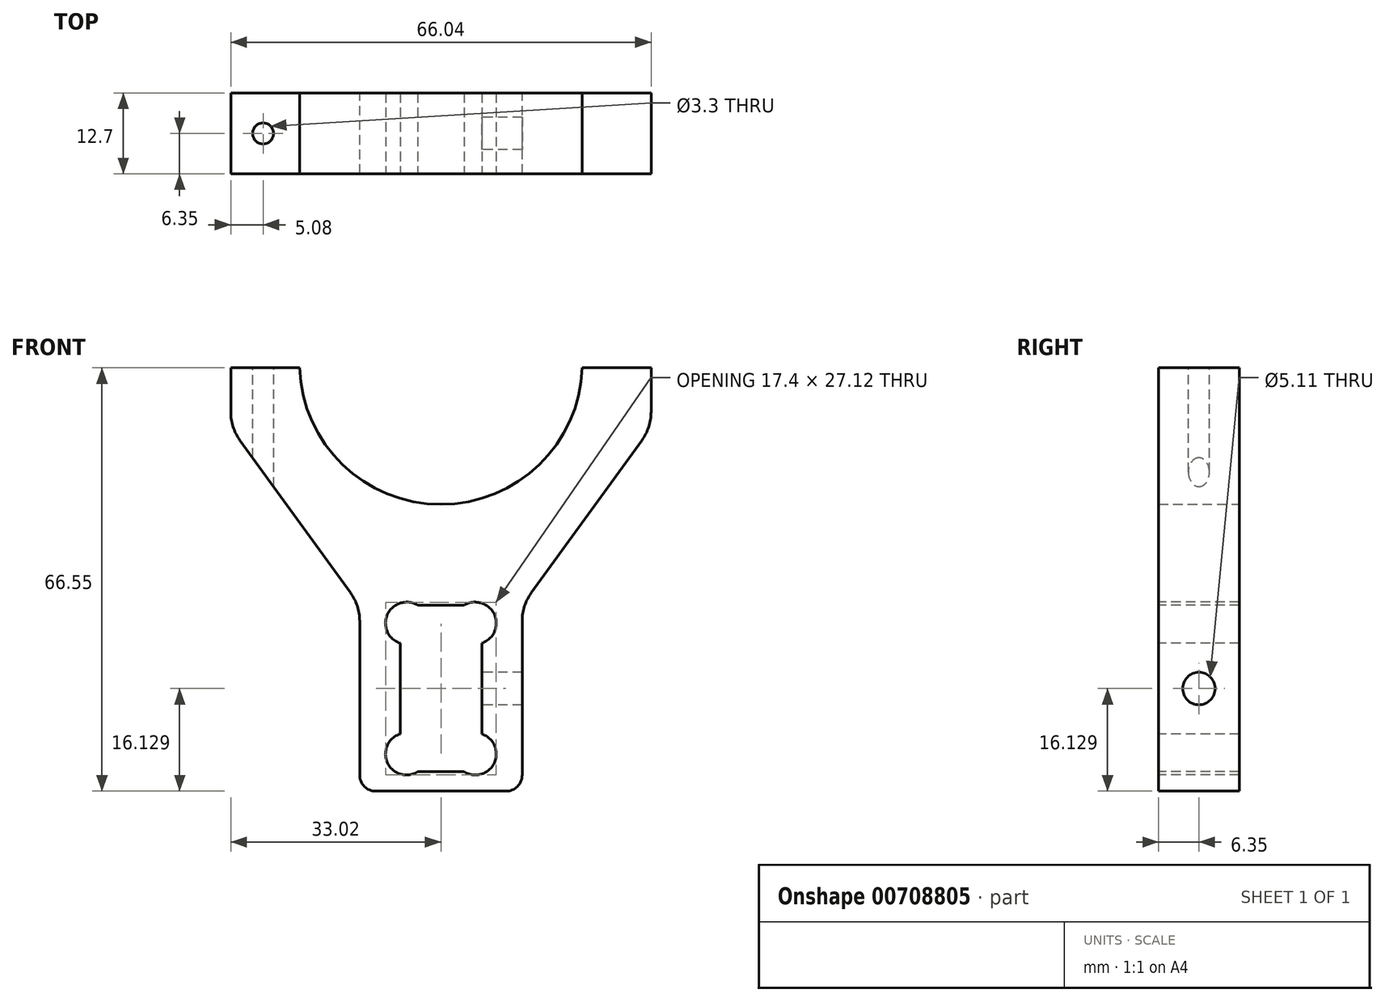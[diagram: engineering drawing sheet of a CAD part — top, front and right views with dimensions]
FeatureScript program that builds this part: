
annotation { "Feature Type Name" : "Feature", "Feature Type Description" : "" }
export const myFeature = defineFeature(function(context is Context, id is Id, definition is map)
    precondition{}
    {
        {
            var Q0;
            Q0=qCreatedBy(makeId("Front.planeOp"),FACE);
            var sketch = newSketch(context, id + "F0", { "sketchPlane" : qUnion([Q0])});
            skLineSegment(sketch, "E0", {"start": v(-6.41, 0) * mm, "end": v(6.41, 0) * mm});
            skLineSegment(sketch, "E1", {"start": v(6.41, 0) * mm, "end": v(6.41, -26.16) * mm});
            skLineSegment(sketch, "E2", {"start": v(12.76, -29.21) * mm, "end": v(12.76, 0) * mm});
            skLineSegment(sketch, "E3", {"start": v(-12.76, 0) * mm, "end": v(-12.76, -29.21) * mm});
            skLineSegment(sketch, "E4", {"start": v(-12.76, -29.21) * mm, "end": v(12.76, -29.21) * mm});
            skLineSegment(sketch, "E5", {"start": v(6.41, -26.16) * mm, "end": v(-6.41, -26.16) * mm});
            skLineSegment(sketch, "E6", {"start": v(-6.41, -26.16) * mm, "end": v(-6.41, 0) * mm});
            skCircle(sketch, "E7", {"center": v(0, 38.1) * mm, "radius": 20 * mm, "construction": true});
            skCircle(sketch, "E8", {"center": v(0, 38.1) * mm, "radius": 32.5 * mm, "construction": true});
            skLineSegment(sketch, "E9", {"start": v(-22.21, 37.34) * mm, "end": v(-33.02, 37.34) * mm});
            skLineSegment(sketch, "E10", {"start": v(-33.02, 37.34) * mm, "end": v(-33.02, 27.94) * mm});
            skLineSegment(sketch, "E11", {"start": v(-33.02, 27.94) * mm, "end": v(-12.76, 0) * mm});
            skLineSegment(sketch, "E12.MirrorCS", {"start": v(33.02, 27.94) * mm, "end": v(12.76, 0) * mm});
            skLineSegment(sketch, "E13.MirrorCS", {"start": v(22.21, 37.34) * mm, "end": v(33.02, 37.34) * mm});
            skLineSegment(sketch, "E14.MirrorCS", {"start": v(33.02, 37.34) * mm, "end": v(33.02, 27.94) * mm});
            skArc(sketch, "E15", {"start": v(-22.21, 37.34) * mm, "mid": v(0, 15.88) * mm, "end": v(22.21, 37.34) * mm});
            skArc(sketch, "E16", {"start": v(22.21, 37.34) * mm, "mid": v(0, 60.33) * mm, "end": v(-22.21, 37.34) * mm, "construction": true});
            skSolve(sketch);
        }
        {
            var Q0;
            Q0 = qSketchRegion(id + "F0", true);
            extrude(context, id + "F1", {"entities" : qUnion([Q0]), "endBound" : BoundingType.SYMMETRIC, "depth" : 12.7 * mm, "offsetDistance" : 25.4 * mm});
        }
        {
            var Q0;
            Q0=makeQuery(id+"F1.opExtrude","SWEPT_FACE",FACE,{"disambiguationData":[OSD([sQuery(id+"F0.wireOp",EDGE,"E1")])]});
            var sketch = newSketch(context, id + "F2", { "sketchPlane" : qUnion([Q0])});
            skPoint(sketch, "E17", {"position": v(0, -13.08) * mm});
            skPoint(sketch, "E17.positionSnap0", {"position": v(6.35, -13.08) * mm});
            skSolve(sketch);
        }
        {
            var Q0;
            Q0=sQuery(id+"F2.wireOp",VERTEX,"E17");
            var Q1;
            Q1=makeQuery(id+"F1.opExtrude","SWEPT_BODY",BODY,{"disambiguationData":[OSD([sQuery(id+"F0.wireOp",EDGE,"E0"),sQuery(id+"F0.wireOp",EDGE,"E1"),sQuery(id+"F0.wireOp",EDGE,"ni5wsZpV-8p3O-xFn4-o8eJ-9v3oh6C6cNDv"),sQuery(id+"F0.wireOp",EDGE,"E2"),sQuery(id+"F0.wireOp",EDGE,"E3"),sQuery(id+"F0.wireOp",EDGE,"E4"),sQuery(id+"F0.wireOp",EDGE,"nnjwPbS3-Dbt6-o5mY-sgKg-kmcwQRUzXATD"),sQuery(id+"F0.wireOp",EDGE,"E5"),sQuery(id+"F0.wireOp",EDGE,"E6"),sQuery(id+"F0.wireOp",EDGE,"E9"),sQuery(id+"F0.wireOp",EDGE,"E10"),sQuery(id+"F0.wireOp",EDGE,"E11"),sQuery(id+"F0.wireOp",EDGE,"E12.MirrorCS"),sQuery(id+"F0.wireOp",EDGE,"E13.MirrorCS"),sQuery(id+"F0.wireOp",EDGE,"E14.MirrorCS"),sQuery(id+"F0.wireOp",EDGE,"E15")])]});
            hole(context, id + "F3", {"style" : HoleStyle.SIMPLE, "endStyle" : HoleEndStyle.THROUGH, "standardTappedOrClearance" : lookupTablePath({ "standard" : "ANSI", "engagement" : "75%", "pitch" : "20 tpi", "size" : "1/4", "type" : "Tapped" }), "standardBlindInLast" : lookupTablePath({ "standard" : "ANSI", "engagement" : "75%", "pitch" : "20 tpi", "size" : "1/4", "type" : "Tapped" }), "holeDiameter" : 5.1 * mm, "majorDiameter" : 6.35 * mm, "showTappedDepth" : true, "isTappedThrough" : true, "tappedDepth" : 12.7 * mm, "tapClearance" : 3, "locations" : qUnion([Q0]), "scope" : qUnion([Q1])});
        }
        {
            var Q0;
            Q0=makeQuery(id+"F1.opExtrude","SWEPT_FACE",FACE,{"disambiguationData":[OSD([sQuery(id+"F0.wireOp",EDGE,"E9")])]});
            var sketch = newSketch(context, id + "F4", { "sketchPlane" : qUnion([Q0])});
            skPoint(sketch, "E18", {"position": v(-27.94, 0) * mm});
            skSolve(sketch);
        }
        {
            var Q0;
            Q0=sQuery(id+"F4.wireOp",VERTEX,"E18");
            var Q1;
            Q1=makeQuery(id+"F1.opExtrude","SWEPT_BODY",BODY,{"disambiguationData":[OSD([sQuery(id+"F0.wireOp",EDGE,"E0"),sQuery(id+"F0.wireOp",EDGE,"E1"),sQuery(id+"F0.wireOp",EDGE,"ni5wsZpV-8p3O-xFn4-o8eJ-9v3oh6C6cNDv"),sQuery(id+"F0.wireOp",EDGE,"E2"),sQuery(id+"F0.wireOp",EDGE,"E3"),sQuery(id+"F0.wireOp",EDGE,"E4"),sQuery(id+"F0.wireOp",EDGE,"nnjwPbS3-Dbt6-o5mY-sgKg-kmcwQRUzXATD"),sQuery(id+"F0.wireOp",EDGE,"E5"),sQuery(id+"F0.wireOp",EDGE,"E6"),sQuery(id+"F0.wireOp",EDGE,"E9"),sQuery(id+"F0.wireOp",EDGE,"E10"),sQuery(id+"F0.wireOp",EDGE,"E11"),sQuery(id+"F0.wireOp",EDGE,"E12.MirrorCS"),sQuery(id+"F0.wireOp",EDGE,"E13.MirrorCS"),sQuery(id+"F0.wireOp",EDGE,"E14.MirrorCS"),sQuery(id+"F0.wireOp",EDGE,"E15")])]});
            hole(context, id + "F5", {"style" : HoleStyle.SIMPLE, "endStyle" : HoleEndStyle.THROUGH, "standardTappedOrClearance" : lookupTablePath({ "standard" : "ISO", "engagement" : "75%", "pitch" : "0.7 mm", "size" : "M4", "type" : "Tapped" }), "standardBlindInLast" : lookupTablePath({ "standard" : "ISO", "engagement" : "75%", "pitch" : "0.7 mm", "size" : "M4", "type" : "Tapped" }), "holeDiameter" : 3.3 * mm, "majorDiameter" : 4 * mm, "showTappedDepth" : true, "isTappedThrough" : true, "tappedDepth" : 12.7 * mm, "tapClearance" : 5, "locations" : qUnion([Q0]), "scope" : qUnion([Q1])});
        }
        {
            var Q0;
            Q0=makeQuery(id+"F1.opExtrude","CAP_FACE",FACE,{"disambiguationData":[OSD([sQuery(id+"F0.wireOp",EDGE,"E0"),sQuery(id+"F0.wireOp",EDGE,"E1"),sQuery(id+"F0.wireOp",EDGE,"ni5wsZpV-8p3O-xFn4-o8eJ-9v3oh6C6cNDv"),sQuery(id+"F0.wireOp",EDGE,"E2"),sQuery(id+"F0.wireOp",EDGE,"E3"),sQuery(id+"F0.wireOp",EDGE,"E4"),sQuery(id+"F0.wireOp",EDGE,"nnjwPbS3-Dbt6-o5mY-sgKg-kmcwQRUzXATD"),sQuery(id+"F0.wireOp",EDGE,"E5"),sQuery(id+"F0.wireOp",EDGE,"E6"),sQuery(id+"F0.wireOp",EDGE,"E9"),sQuery(id+"F0.wireOp",EDGE,"E10"),sQuery(id+"F0.wireOp",EDGE,"E11"),sQuery(id+"F0.wireOp",EDGE,"E12.MirrorCS"),sQuery(id+"F0.wireOp",EDGE,"E13.MirrorCS"),sQuery(id+"F0.wireOp",EDGE,"E14.MirrorCS"),sQuery(id+"F0.wireOp",EDGE,"E15")])],"isStart":false});
            var sketch = newSketch(context, id + "F6", { "sketchPlane" : qUnion([Q0])});
            skCircle(sketch, "E19", {"center": v(-5.4, -2.8) * mm, "radius": 3.3 * mm});
            skCircle(sketch, "E20", {"center": v(-5.4, -23.37) * mm, "radius": 3.3 * mm});
            skCircle(sketch, "E21", {"center": v(5.4, -2.8) * mm, "radius": 3.3 * mm});
            skCircle(sketch, "E22", {"center": v(5.4, -23.37) * mm, "radius": 3.3 * mm});
            skSolve(sketch);
        }
        {
            var Q0;
            Q0 = qSketchRegion(id + "F6", true);
            extrude(context, id + "F7", {"entities" : qUnion([Q0]), "operationType" : NewBodyOperationType.REMOVE, "endBound" : BoundingType.THROUGH_ALL, "oppositeDirection" : true, "depth" : 25.4 * mm, "offsetDistance" : 25.4 * mm});
        }
        {
            var Q0;
            Q0=makeQuery(id+"F1.opExtrude","SWEPT_EDGE",EDGE,{"disambiguationData":[OSD([sQuery(id+"F0.wireOp",EDGE,"E2"),sQuery(id+"F0.wireOp",EDGE,"E4")])]});
            var Q1;
            Q1=makeQuery(id+"F1.opExtrude","SWEPT_EDGE",EDGE,{"disambiguationData":[OSD([sQuery(id+"F0.wireOp",EDGE,"E3"),sQuery(id+"F0.wireOp",EDGE,"E4")])]});
            fillet(context, id + "F8", {"entities" : qUnion([Q0, Q1]), "radius" : 2.54 * mm, "tangentPropagation" : true, "allowEdgeOverflow" : false});
        }
        {
            var Q0;
            Q0=makeQuery(id+"F1.opExtrude","SWEPT_EDGE",EDGE,{"disambiguationData":[OSD([sQuery(id+"F0.wireOp",EDGE,"E2"),sQuery(id+"F0.wireOp",EDGE,"E12.MirrorCS")])]});
            var Q1;
            Q1=makeQuery(id+"F1.opExtrude","SWEPT_EDGE",EDGE,{"disambiguationData":[OSD([sQuery(id+"F0.wireOp",EDGE,"E3"),sQuery(id+"F0.wireOp",EDGE,"E11")])]});
            fillet(context, id + "F9", {"entities" : qUnion([Q0, Q1]), "radius" : 7.62 * mm, "tangentPropagation" : true, "allowEdgeOverflow" : false});
        }
        {
            var Q0;
            Q0=makeQuery(id+"F1.opExtrude","SWEPT_EDGE",EDGE,{"disambiguationData":[OSD([sQuery(id+"F0.wireOp",EDGE,"E12.MirrorCS"),sQuery(id+"F0.wireOp",EDGE,"E14.MirrorCS")])]});
            var Q1;
            Q1=makeQuery(id+"F1.opExtrude","SWEPT_EDGE",EDGE,{"disambiguationData":[OSD([sQuery(id+"F0.wireOp",EDGE,"E10"),sQuery(id+"F0.wireOp",EDGE,"E11")])]});
            fillet(context, id + "F10", {"entities" : qUnion([Q0, Q1]), "radius" : 7.62 * mm, "tangentPropagation" : true, "allowEdgeOverflow" : false});
        }
    });
